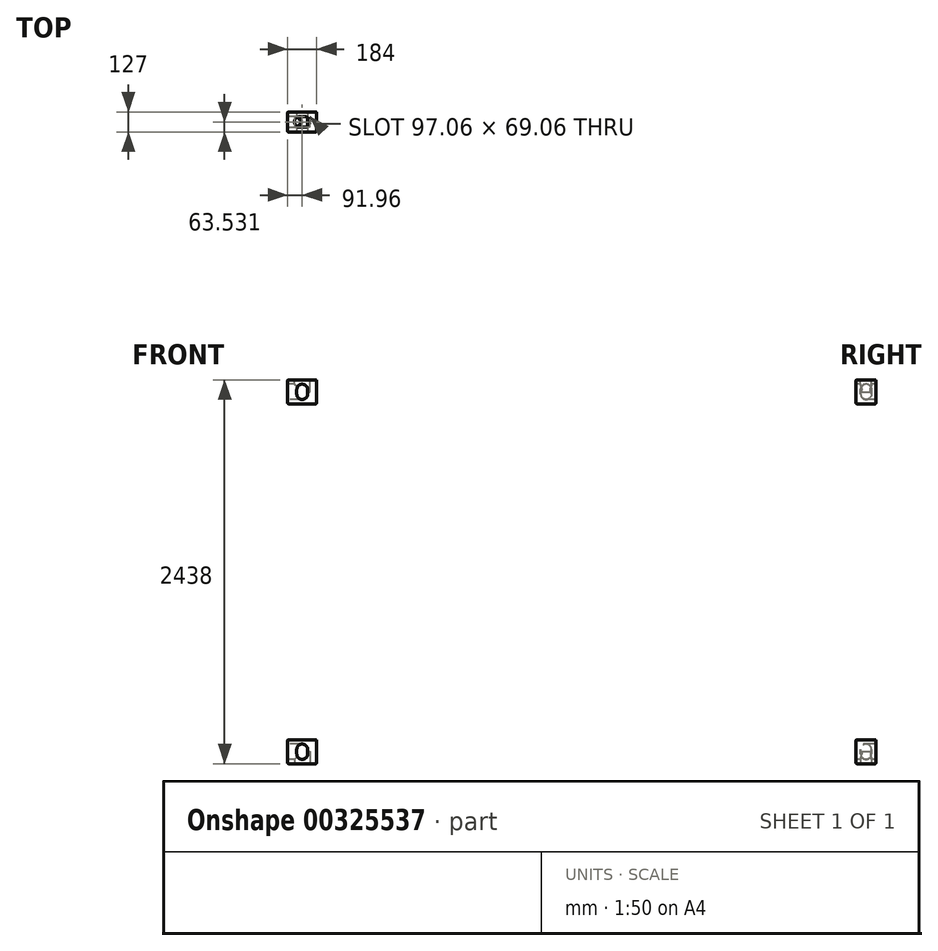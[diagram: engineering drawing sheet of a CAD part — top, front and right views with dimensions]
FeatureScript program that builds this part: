
annotation { "Feature Type Name" : "Feature", "Feature Type Description" : "" }
export const myFeature = defineFeature(function(context is Context, id is Id, definition is map)
    precondition{}
    {
        {
            var Q0;
            Q0=qCreatedBy(makeId("Top.planeOp"),FACE);
            var sketch = newSketch(context, id + "F0", { "sketchPlane" : qUnion([Q0])});
            skLineSegment(sketch, "E0.bottom", {"start": v(-139.35, 105.7) * mm, "end": v(44.65, 105.7) * mm});
            skLineSegment(sketch, "E0.top", {"start": v(-139.35, -21.3) * mm, "end": v(44.65, -21.3) * mm});
            skLineSegment(sketch, "E0.left", {"start": v(-139.35, 105.7) * mm, "end": v(-139.35, -21.3) * mm});
            skLineSegment(sketch, "E0.right", {"start": v(44.65, 105.7) * mm, "end": v(44.65, -21.3) * mm});
            skSolve(sketch);
        }
        {
            var Q0;
            Q0=makeQuery(id+"F0.imprint","IMPRINT",FACE,{"disambiguationData":[TD([[makeQuery(id+"F0.imprint","IMPRINT",EDGE,{"derivedFrom":sQuery(id+"F0.wireOp",EDGE,"E0.bottom")}),-1.0]])]});
            extrude(context, id + "F1", {"entities" : qUnion([Q0]), "depth" : 152 * mm});
        }
        {
            var Q0;
            Q0=makeQuery(id+"F1.opExtrude","SWEPT_FACE",FACE,{"disambiguationData":[OSD([sQuery(id+"F0.wireOp",EDGE,"E0.top")])]});
            var sketch = newSketch(context, id + "F2", { "sketchPlane" : qUnion([Q0])});
            skLineSegment(sketch, "E1", {"start": v(-81.88, 76) * mm, "end": v(-81.88, 90) * mm});
            skArc(sketch, "E2.trimOffspring", {"start": v(-12.82, 90) * mm, "mid": v(-47.35, 124.53) * mm, "end": v(-81.88, 90) * mm});
            skLineSegment(sketch, "E3", {"start": v(-12.82, 90) * mm, "end": v(-12.82, 76) * mm});
            skArc(sketch, "E4.MirrorCS", {"start": v(-12.82, 62) * mm, "mid": v(-47.35, 27.47) * mm, "end": v(-81.88, 62) * mm});
            skLineSegment(sketch, "E5.MirrorCS", {"start": v(-12.82, 62) * mm, "end": v(-12.82, 76) * mm});
            skLineSegment(sketch, "E6.MirrorCS", {"start": v(-81.88, 76) * mm, "end": v(-81.88, 62) * mm});
            skSolve(sketch);
        }
        {
            var Q0;
            Q0=qSketchRegion(id+"F2",true);
            extrude(context, id + "F3", {"entities" : qUnion([Q0]), "operationType" : NewBodyOperationType.REMOVE, "depth" : -122 * mm});
        }
        {
            var Q0;
            Q0=makeQuery(id+"F1.opExtrude","SWEPT_FACE",FACE,{"disambiguationData":[OSD([sQuery(id+"F0.wireOp",EDGE,"E0.left")])]});
            var sketch = newSketch(context, id + "F4", { "sketchPlane" : qUnion([Q0])});
            skLineSegment(sketch, "E7", {"start": v(-76.74, 76.01) * mm, "end": v(-76.74, 90.01) * mm});
            skArc(sketch, "E8.trimOffspring", {"start": v(-7.68, 90.01) * mm, "mid": v(-42.2, 124.54) * mm, "end": v(-76.74, 90.01) * mm});
            skLineSegment(sketch, "E9", {"start": v(-7.68, 90.01) * mm, "end": v(-7.68, 76.01) * mm});
            skArc(sketch, "E10.MirrorCS", {"start": v(-7.68, 62.01) * mm, "mid": v(-42.2, 27.48) * mm, "end": v(-76.74, 62.01) * mm});
            skLineSegment(sketch, "E11.MirrorCS", {"start": v(-7.68, 62.01) * mm, "end": v(-7.68, 76.01) * mm});
            skLineSegment(sketch, "E12.MirrorCS", {"start": v(-76.74, 76.01) * mm, "end": v(-76.74, 62.01) * mm});
            skSolve(sketch);
        }
        {
            var Q0;
            Q0=makeQuery(id+"F4.imprint","IMPRINT",FACE,{"disambiguationData":[TD([[makeQuery(id+"F4.imprint","IMPRINT",EDGE,{"derivedFrom":sQuery(id+"F4.wireOp",EDGE,"E7")}),-1.0]])]});
            extrude(context, id + "F5", {"entities" : qUnion([Q0]), "operationType" : NewBodyOperationType.REMOVE, "oppositeDirection" : true, "depth" : 92 * mm});
        }
        {
            var Q0;
            Q0=makeQuery(id+"F1.opExtrude","CAP_FACE",FACE,{"disambiguationData":[OSD([sQuery(id+"F0.wireOp",EDGE,"E0.bottom"),sQuery(id+"F0.wireOp",EDGE,"E0.top"),sQuery(id+"F0.wireOp",EDGE,"E0.left"),sQuery(id+"F0.wireOp",EDGE,"E0.right")])],"isStart":false});
            var sketch = newSketch(context, id + "F6", { "sketchPlane" : qUnion([Q0])});
            skLineSegment(sketch, "E13", {"start": v(-47.39, 76.77) * mm, "end": v(-33.39, 76.77) * mm});
            skArc(sketch, "E14.trimOffspring", {"start": v(-33.39, 7.7) * mm, "mid": v(1.14, 42.24) * mm, "end": v(-33.39, 76.77) * mm});
            skLineSegment(sketch, "E15", {"start": v(-33.39, 7.7) * mm, "end": v(-47.39, 7.7) * mm});
            skArc(sketch, "E16.MirrorCS", {"start": v(-61.39, 7.7) * mm, "mid": v(-95.92, 42.24) * mm, "end": v(-61.39, 76.77) * mm});
            skLineSegment(sketch, "E17.MirrorCS", {"start": v(-61.39, 7.7) * mm, "end": v(-47.39, 7.7) * mm});
            skLineSegment(sketch, "E18.MirrorCS", {"start": v(-47.39, 76.77) * mm, "end": v(-61.39, 76.77) * mm});
            skSolve(sketch);
        }
        {
            var Q0;
            Q0=qSketchRegion(id+"F6",true);
            extrude(context, id + "F7", {"entities" : qUnion([Q0]), "operationType" : NewBodyOperationType.REMOVE, "oppositeDirection" : true, "depth" : 78 * mm});
        }
        {
            var Q0;
            Q0=makeQuery(id+"F1.opExtrude","CAP_EDGE",EDGE,{"disambiguationData":[OSD([sQuery(id+"F0.wireOp",EDGE,"E0.top")])],"isStart":false});
            fillet(context, id + "F8", {"entities" : qUnion([Q0]), "radius" : 5 * mm, "tangentPropagation" : true, "allowEdgeOverflow" : false});
        }
        {
            var Q0;
            Q0=makeQuery(id+"F1.opExtrude","SWEPT_EDGE",EDGE,{"disambiguationData":[OSD([sQuery(id+"F0.wireOp",EDGE,"E0.top"),sQuery(id+"F0.wireOp",EDGE,"E0.left")])]});
            var Q1;
            Q1=makeQuery(id+"F1.opExtrude","CAP_EDGE",EDGE,{"disambiguationData":[OSD([sQuery(id+"F0.wireOp",EDGE,"E0.left")])],"isStart":false});
            var Q2;
            Q2=makeQuery(id+"F1.opExtrude","CAP_EDGE",EDGE,{"disambiguationData":[OSD([sQuery(id+"F0.wireOp",EDGE,"E0.right")])],"isStart":false});
            var Q3;
            Q3=makeQuery(id+"F1.opExtrude","CAP_EDGE",EDGE,{"disambiguationData":[OSD([sQuery(id+"F0.wireOp",EDGE,"E0.bottom")])],"isStart":false});
            var Q4;
            Q4=makeQuery(id+"F1.opExtrude","SWEPT_EDGE",EDGE,{"disambiguationData":[OSD([sQuery(id+"F0.wireOp",EDGE,"E0.top"),sQuery(id+"F0.wireOp",EDGE,"E0.right")])]});
            var Q5;
            Q5=makeQuery(id+"F1.opExtrude","CAP_EDGE",EDGE,{"disambiguationData":[OSD([sQuery(id+"F0.wireOp",EDGE,"E0.top")])],"isStart":true});
            fillet(context, id + "F9", {"entities" : qUnion([Q0, Q1, Q2, Q3, Q4, Q5]), "radius" : 5 * mm, "tangentPropagation" : true, "allowEdgeOverflow" : false});
        }
        {
            var Q0;
            Q0=makeQuery(id+"F1.opExtrude","SWEPT_EDGE",EDGE,{"disambiguationData":[OSD([sQuery(id+"F0.wireOp",EDGE,"E0.bottom"),sQuery(id+"F0.wireOp",EDGE,"E0.left")])]});
            var Q1;
            Q1=makeQuery(id+"F1.opExtrude","SWEPT_EDGE",EDGE,{"disambiguationData":[OSD([sQuery(id+"F0.wireOp",EDGE,"E0.bottom"),sQuery(id+"F0.wireOp",EDGE,"E0.right")])]});
            var Q2;
            Q2=makeQuery(id+"F1.opExtrude","CAP_EDGE",EDGE,{"disambiguationData":[OSD([sQuery(id+"F0.wireOp",EDGE,"E0.bottom")])],"isStart":true});
            var Q3;
            Q3=makeQuery(id+"F1.opExtrude","CAP_EDGE",EDGE,{"disambiguationData":[OSD([sQuery(id+"F0.wireOp",EDGE,"E0.right")])],"isStart":true});
            fillet(context, id + "F10", {"entities" : qUnion([Q0, Q1, Q2, Q3]), "radius" : 5 * mm, "tangentPropagation" : true, "allowEdgeOverflow" : false});
        }
        {
            var Q0;
            Q0=makeQuery(id+"F1.opExtrude","CAP_EDGE",EDGE,{"disambiguationData":[OSD([sQuery(id+"F0.wireOp",EDGE,"E0.left")])],"isStart":true});
            fillet(context, id + "F11", {"entities" : qUnion([Q0]), "radius" : 5 * mm, "tangentPropagation" : true, "allowEdgeOverflow" : false});
        }
        {
            var Q0;
            Q0=qCreatedBy(makeId("Top.planeOp"),FACE);
            cPlane(context, id + "F12", {"entities" : qUnion([Q0]), "cplaneType" : CPlaneType.OFFSET, "offset" : 1067 * mm, "oppositeDirection" : true, "width" : 150 * mm, "height" : 150 * mm});
        }
        {
            var Q0;
            Q0=makeQuery(id+"F1.opExtrude","SWEPT_BODY",BODY,{"disambiguationData":[OSD([sQuery(id+"F0.wireOp",EDGE,"E0.bottom"),sQuery(id+"F0.wireOp",EDGE,"E0.top"),sQuery(id+"F0.wireOp",EDGE,"E0.left"),sQuery(id+"F0.wireOp",EDGE,"E0.right")])]});
            var Q1;
            Q1=qCreatedBy(id+"F12.planeOp",FACE);
            mirror(context, id + "F13", {"entities" : qUnion([Q0]), "mirrorPlane" : qUnion([Q1])});
        }
    });
